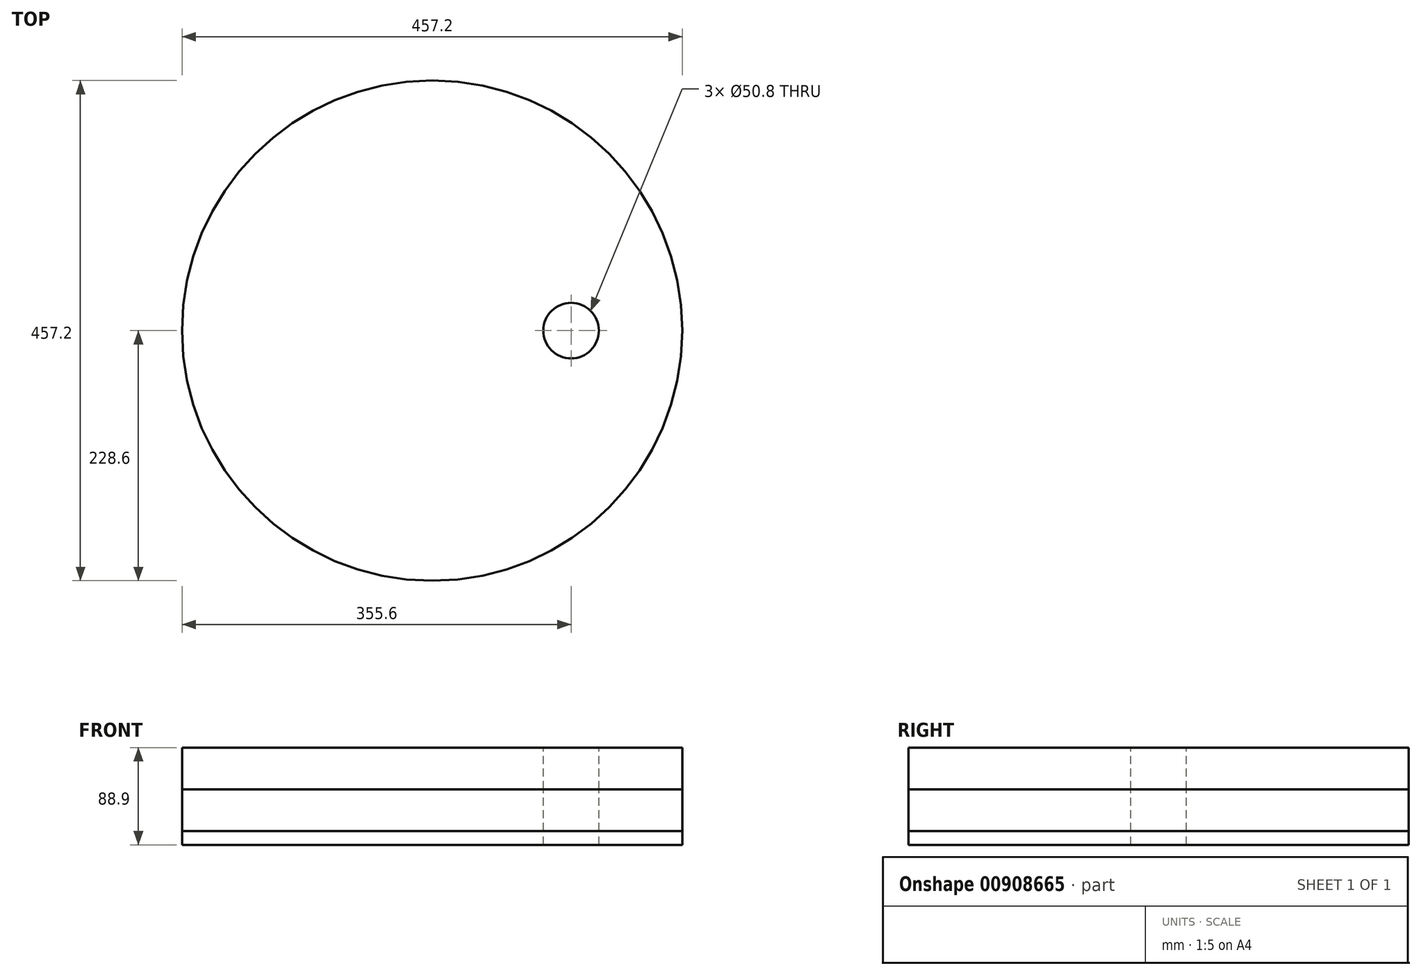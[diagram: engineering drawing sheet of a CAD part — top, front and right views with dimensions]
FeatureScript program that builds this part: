
annotation { "Feature Type Name" : "Feature", "Feature Type Description" : "" }
export const myFeature = defineFeature(function(context is Context, id is Id, definition is map)
    precondition{}
    {
        {
            var Q0;
            Q0=qCreatedBy(makeId("Top.planeOp"),FACE);
            var sketch = newSketch(context, id + "F0", { "sketchPlane" : qUnion([Q0])});
            skCircle(sketch, "E0", {"center": v(0, 0) * mm, "radius": 228.6 * mm});
            skSolve(sketch);
        }
        {
            var Q0;
            Q0=qSketchRegion(id+"F0",true);
            extrude(context, id + "F1", {"entities" : qUnion([Q0]), "depth" : 12.7 * mm, "offsetDistance" : 25.4 * mm});
        }
        {
            var Q0;
            Q0=makeQuery(id+"F1.opExtrude","CAP_FACE",FACE,{"disambiguationData":[OSD([sQuery(id+"F0.wireOp",EDGE,"E0")])],"isStart":false});
            extrude(context, id + "F2", {"entities" : qUnion([Q0]), "depth" : 38.1 * mm, "offsetDistance" : 25.4 * mm});
        }
        {
            var Q0;
            Q0=makeQuery(id+"F2.opExtrude","CAP_FACE",FACE,{"disambiguationData":[OSD([sQuery(id+"F0.wireOp",EDGE,"E0")])],"isStart":false});
            extrude(context, id + "F3", {"entities" : qUnion([Q0]), "depth" : 38.1 * mm, "offsetDistance" : 25.4 * mm});
        }
        {
            var Q0;
            Q0=makeQuery(id+"F3.opExtrude","CAP_FACE",FACE,{"disambiguationData":[OSD([sQuery(id+"F0.wireOp",EDGE,"E0")])],"isStart":false});
            var sketch = newSketch(context, id + "F4", { "sketchPlane" : qUnion([Q0])});
            skCircle(sketch, "E1", {"center": v(127, 0) * mm, "radius": 25.4 * mm});
            skSolve(sketch);
        }
        {
            var Q0;
            Q0=qSketchRegion(id+"F4",true);
            extrude(context, id + "F5", {"entities" : qUnion([Q0]), "operationType" : NewBodyOperationType.REMOVE, "endBound" : BoundingType.THROUGH_ALL, "oppositeDirection" : true, "depth" : 25.4 * mm, "offsetDistance" : 25.4 * mm});
        }
    });
